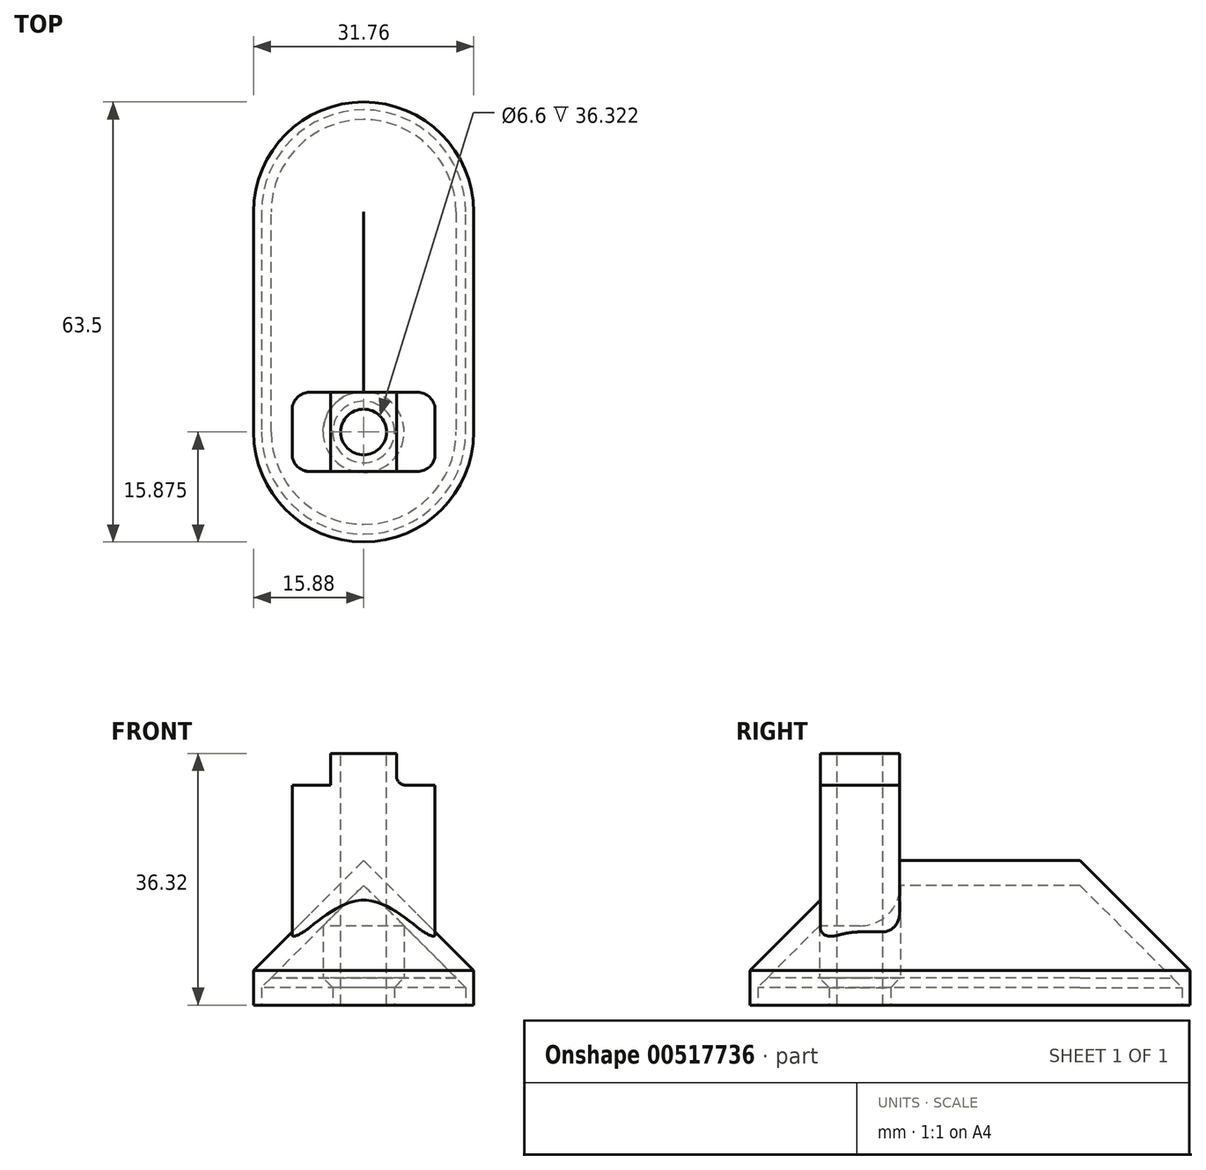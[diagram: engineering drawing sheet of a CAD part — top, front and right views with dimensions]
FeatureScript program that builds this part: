
annotation { "Feature Type Name" : "Feature", "Feature Type Description" : "" }
export const myFeature = defineFeature(function(context is Context, id is Id, definition is map)
    precondition{}
    {
        {
            var Q0;
            Q0=qCreatedBy(makeId("Top.planeOp"),FACE);
            var sketch = newSketch(context, id + "F0", { "sketchPlane" : qUnion([Q0])});
            skLineSegment(sketch, "E0.left", {"start": v(15.88, -15.88) * mm, "end": v(15.88, 15.88) * mm});
            skLineSegment(sketch, "E0.right", {"start": v(-15.88, -15.88) * mm, "end": v(-15.88, 15.87) * mm});
            skPoint(sketch, "E0.middle", {"position": v(0, 0) * mm});
            skArc(sketch, "E1", {"start": v(-15.88, -15.88) * mm, "mid": v(0, -31.75) * mm, "end": v(15.87, -15.88) * mm});
            skArc(sketch, "E2", {"start": v(15.87, 15.88) * mm, "mid": v(0, 31.75) * mm, "end": v(-15.88, 15.88) * mm});
            skSolve(sketch);
        }
        {
            var Q0;
            Q0=makeQuery(id+"F0.imprint","IMPRINT",FACE,{"disambiguationData":[TD([[makeQuery(id+"F0.imprint","IMPRINT",EDGE,{"derivedFrom":sQuery(id+"F0.wireOp",EDGE,"E0.left")}),1.0]])]});
            extrude(context, id + "F1", {"entities" : qUnion([Q0]), "depth" : 20.87 * mm, "offsetDistance" : 25.4 * mm});
        }
        {
            var Q0;
            Q0=makeQuery(id+"F1.opExtrude","CAP_EDGE",EDGE,{"disambiguationData":[OSD([sQuery(id+"F0.wireOp",EDGE,"E0.left")])],"isStart":false});
            chamfer(context, id + "F2", {"entities" : qUnion([Q0]), "width" : 15.88 * mm, "tangentPropagation" : true});
        }
        {
            var Q0;
            Q0=qCreatedBy(makeId("Top.planeOp"),FACE);
            cPlane(context, id + "F3", {"entities" : qUnion([Q0]), "cplaneType" : CPlaneType.OFFSET, "offset" : 31.75 * mm, "width" : 152.4 * mm, "height" : 152.4 * mm});
        }
        {
            var Q0;
            Q0=makeQuery(id+"F1.opExtrude","CAP_FACE",FACE,{"disambiguationData":[OSD([sQuery(id+"F0.wireOp",EDGE,"E0.left"),sQuery(id+"F0.wireOp",EDGE,"E0.right"),sQuery(id+"F0.wireOp",EDGE,"E1"),sQuery(id+"F0.wireOp",EDGE,"E2")])],"isStart":true});
            shell(context, id + "F4", {"entities" : qUnion([Q0]), "thickness" : 2.54 * mm});
        }
        {
            var Q0;
            Q0=qCreatedBy(id+"F3.planeOp",FACE);
            var sketch = newSketch(context, id + "F5", { "sketchPlane" : qUnion([Q0])});
            skLineSegment(sketch, "E3.bottom", {"start": v(10.31, -21.6) * mm, "end": v(-10.31, -21.6) * mm});
            skLineSegment(sketch, "E3.top", {"start": v(10.31, -10.16) * mm, "end": v(-10.31, -10.16) * mm});
            skLineSegment(sketch, "E3.left", {"start": v(10.31, -21.6) * mm, "end": v(10.31, -10.16) * mm});
            skLineSegment(sketch, "E3.right", {"start": v(-10.31, -21.6) * mm, "end": v(-10.31, -10.16) * mm});
            skPoint(sketch, "E3.middle", {"position": v(0, -15.88) * mm});
            skSolve(sketch);
        }
        {
            var Q0;
            Q0=makeQuery(id+"F5.imprint","IMPRINT",FACE,{"disambiguationData":[TD([[makeQuery(id+"F5.imprint","IMPRINT",EDGE,{"derivedFrom":sQuery(id+"F5.wireOp",EDGE,"E3.bottom")}),-1.0]])]});
            extrude(context, id + "F6", {"entities" : qUnion([Q0]), "operationType" : NewBodyOperationType.ADD, "endBound" : BoundingType.UP_TO_NEXT, "oppositeDirection" : true, "depth" : 25.4 * mm, "offsetDistance" : 25.4 * mm});
        }
        {
            var Q0;
            Q0=makeQuery(id+"F6.opExtrude","CAP_FACE",FACE,{"disambiguationData":[OSD([sQuery(id+"F5.wireOp",EDGE,"E3.bottom"),sQuery(id+"F5.wireOp",EDGE,"E3.top"),sQuery(id+"F5.wireOp",EDGE,"E3.left"),sQuery(id+"F5.wireOp",EDGE,"E3.right")])],"isStart":true});
            var sketch = newSketch(context, id + "F7", { "sketchPlane" : qUnion([Q0])});
            skLineSegment(sketch, "E4.bottom", {"start": v(4.76, -10.16) * mm, "end": v(-4.76, -10.16) * mm});
            skLineSegment(sketch, "E4.top", {"start": v(4.76, -21.6) * mm, "end": v(-4.76, -21.6) * mm});
            skLineSegment(sketch, "E4.left", {"start": v(4.76, -10.16) * mm, "end": v(4.76, -21.6) * mm});
            skLineSegment(sketch, "E4.right", {"start": v(-4.76, -10.16) * mm, "end": v(-4.76, -21.6) * mm});
            skPoint(sketch, "E4.middle", {"position": v(0, -15.88) * mm});
            skSolve(sketch);
        }
        {
            var Q0;
            Q0 = qSketchRegion(id + "F7", true);
            extrude(context, id + "F8", {"entities" : qUnion([Q0]), "operationType" : NewBodyOperationType.ADD, "depth" : 4.57 * mm, "offsetDistance" : 25.4 * mm});
        }
        {
            var Q0;
            Q0=makeQuery(id+"F8.opExtrude","CAP_FACE",FACE,{"disambiguationData":[OSD([sQuery(id+"F7.wireOp",EDGE,"E4.bottom"),sQuery(id+"F7.wireOp",EDGE,"E4.top"),sQuery(id+"F7.wireOp",EDGE,"E4.left"),sQuery(id+"F7.wireOp",EDGE,"E4.right")])],"isStart":false});
            var sketch = newSketch(context, id + "F9", { "sketchPlane" : qUnion([Q0])});
            skCircle(sketch, "E5", {"center": v(0, -15.88) * mm, "radius": 3.3 * mm});
            skLineSegment(sketch, "E6", {"start": v(-4.76, -21.6) * mm, "end": v(4.76, -10.16) * mm, "construction": true});
            skSolve(sketch);
        }
        {
            var Q0;
            Q0 = qSketchRegion(id + "F9", true);
            extrude(context, id + "F10", {"entities" : qUnion([Q0]), "operationType" : NewBodyOperationType.REMOVE, "endBound" : BoundingType.THROUGH_ALL, "oppositeDirection" : true, "depth" : 25.4 * mm, "offsetDistance" : 25.4 * mm});
        }
        {
            var Q0;
            Q0=makeQuery(id+"F6.opExtrude","CAP_EDGE",EDGE,{"disambiguationData":[OSD([sQuery(id+"F5.wireOp",EDGE,"E3.right")]),topologyDisambiguationEdgeConnected([makeQuery(id+"F2.opChamfer","BLEND_FACE",FACE,{"disambiguationData":[OSD([sQuery(id+"F0.wireOp",EDGE,"E1")])]})])],"isStart":false});
            var Q1;
            Q1=makeQuery(id+"F6.opExtrude","CAP_EDGE",EDGE,{"disambiguationData":[OSD([sQuery(id+"F5.wireOp",EDGE,"E3.bottom")])],"isStart":false});
            var Q2;
            Q2=makeQuery(id+"F6.opExtrude","CAP_EDGE",EDGE,{"disambiguationData":[OSD([sQuery(id+"F5.wireOp",EDGE,"E3.left")]),topologyDisambiguationEdgeConnected([makeQuery(id+"F2.opChamfer","BLEND_FACE",FACE,{"disambiguationData":[OSD([sQuery(id+"F0.wireOp",EDGE,"E1")])]})])],"isStart":false});
            var Q3;
            Q3=makeQuery(id+"F6.opExtrude","CAP_EDGE",EDGE,{"disambiguationData":[OSD([sQuery(id+"F5.wireOp",EDGE,"E3.top")]),topologyDisambiguationEdgeConnected([makeQuery(id+"F2.opChamfer","BLEND_FACE",FACE,{"disambiguationData":[OSD([sQuery(id+"F0.wireOp",EDGE,"E0.left")])]})])],"isStart":false});
            var Q4;
            Q4=makeQuery(id+"F6.opExtrude","CAP_EDGE",EDGE,{"disambiguationData":[OSD([sQuery(id+"F5.wireOp",EDGE,"E3.top")]),topologyDisambiguationEdgeConnected([makeQuery(id+"F2.opChamfer","BLEND_FACE",FACE,{"disambiguationData":[OSD([sQuery(id+"F0.wireOp",EDGE,"E0.right")])]})])],"isStart":false});
            var Q5;
            Q5=makeQuery(id+"F6.opExtrude","SWEPT_EDGE",EDGE,{"disambiguationData":[OSD([sQuery(id+"F5.wireOp",EDGE,"E3.bottom"),sQuery(id+"F5.wireOp",EDGE,"E3.left")])]});
            var Q6;
            Q6=makeQuery(id+"F6.opExtrude","SWEPT_EDGE",EDGE,{"disambiguationData":[OSD([sQuery(id+"F5.wireOp",EDGE,"E3.top"),sQuery(id+"F5.wireOp",EDGE,"E3.left")])]});
            var Q7;
            Q7=makeQuery(id+"F6.opExtrude","SWEPT_EDGE",EDGE,{"disambiguationData":[OSD([sQuery(id+"F5.wireOp",EDGE,"E3.bottom"),sQuery(id+"F5.wireOp",EDGE,"E3.right")])]});
            var Q8;
            Q8=makeQuery(id+"F6.opExtrude","SWEPT_EDGE",EDGE,{"disambiguationData":[OSD([sQuery(id+"F5.wireOp",EDGE,"E3.top"),sQuery(id+"F5.wireOp",EDGE,"E3.right")])]});
            fillet(context, id + "F11", {"entities" : qUnion([Q0, Q1, Q2, Q3, Q4, Q5, Q6, Q7, Q8]), "radius" : 2.54 * mm, "tangentPropagation" : true, "allowEdgeOverflow" : false});
        }
        {
            var Q0;
            Q0=makeQuery(id+"F1.opExtrude","CAP_FACE",FACE,{"disambiguationData":[OSD([sQuery(id+"F0.wireOp",EDGE,"E0.left"),sQuery(id+"F0.wireOp",EDGE,"E0.right"),sQuery(id+"F0.wireOp",EDGE,"E1"),sQuery(id+"F0.wireOp",EDGE,"E2")])],"isStart":true});
            var sketch = newSketch(context, id + "F12", { "sketchPlane" : qUnion([Q0])});
            skCircle(sketch, "E7", {"center": v(0, 15.88) * mm, "radius": 3.3 * mm});
            skCircle(sketch, "E8", {"center": v(0, 15.88) * mm, "radius": 5.84 * mm});
            skSolve(sketch);
        }
        {
            var Q0;
            Q0=makeQuery(id+"F12.imprint","IMPRINT",FACE,{"disambiguationData":[TD([[makeQuery(id+"F12.imprint","IMPRINT",EDGE,{"derivedFrom":sQuery(id+"F12.wireOp",EDGE,"E7")}),-1.0]])]});
            extrude(context, id + "F13", {"entities" : qUnion([Q0]), "operationType" : NewBodyOperationType.ADD, "endBound" : BoundingType.UP_TO_NEXT, "oppositeDirection" : true, "depth" : 25.4 * mm, "offsetDistance" : 25.4 * mm});
        }
        {
            var Q0;
            Q0=makeQuery(id+"F0.imprint","IMPRINT",FACE,{"disambiguationData":[TD([[makeQuery(id+"F0.imprint","IMPRINT",EDGE,{"derivedFrom":sQuery(id+"F0.wireOp",EDGE,"E0.left")}),1.0]])]});
            var sketch = newSketch(context, id + "F14", { "sketchPlane" : qUnion([Q0])});
            skLineSegment(sketch, "E9", {"start": v(-14.73, 15.88) * mm, "end": v(-14.73, -15.88) * mm});
            skArc(sketch, "E10", {"start": v(-14.73, -15.88) * mm, "mid": v(0, -30.6) * mm, "end": v(14.73, -15.88) * mm});
            skLineSegment(sketch, "E11", {"start": v(14.73, -15.88) * mm, "end": v(14.73, 15.88) * mm});
            skArc(sketch, "E12", {"start": v(14.73, 15.88) * mm, "mid": v(0, 30.6) * mm, "end": v(-14.73, 15.88) * mm});
            skCircle(sketch, "E13", {"center": v(0, -15.88) * mm, "radius": 4.45 * mm});
            skSolve(sketch);
        }
        {
            var Q0;
            Q0 = qSketchRegion(id + "F14", true);
            extrude(context, id + "F15", {"entities" : qUnion([Q0]), "operationType" : NewBodyOperationType.REMOVE, "depth" : 2.54 * mm, "offsetDistance" : 25.4 * mm});
        }
        {
            var Q0;
            {var subQ0=sQuery(id+"F0.wireOp",EDGE,"E0.right");Q0=makeQuery(id+"F15.boolean.opBoolean","INTERSECT",EDGE,{"derivedFrom":[makeQuery(id+"F4.opShell","OFFSET_FACE",FACE,{"disambiguationData":[OSD([subQ0]),TDD([makeQuery(id+"F1.opExtrude","SWEPT_FACE",FACE,{"disambiguationData":[OSD([subQ0])]})])]}),makeQuery(id+"F15.opExtrude","CAP_FACE",FACE,{"disambiguationData":[OSD([sQuery(id+"F14.wireOp",EDGE,"E9"),sQuery(id+"F14.wireOp",EDGE,"E10"),sQuery(id+"F14.wireOp",EDGE,"E11"),sQuery(id+"F14.wireOp",EDGE,"E12"),sQuery(id+"F14.wireOp",EDGE,"E13")])],"isStart":false})]});}
            var Q1;
            Q1=makeQuery(id+"F15.boolean.opBoolean","INTERSECT",EDGE,{"derivedFrom":[makeQuery(id+"F13.opExtrude","SWEPT_FACE",FACE,{"disambiguationData":[OSD([sQuery(id+"F12.wireOp",EDGE,"E8")])]}),makeQuery(id+"F15.opExtrude","CAP_FACE",FACE,{"disambiguationData":[OSD([sQuery(id+"F14.wireOp",EDGE,"E9"),sQuery(id+"F14.wireOp",EDGE,"E10"),sQuery(id+"F14.wireOp",EDGE,"E11"),sQuery(id+"F14.wireOp",EDGE,"E12"),sQuery(id+"F14.wireOp",EDGE,"E13")])],"isStart":false})]});
            chamfer(context, id + "F16", {"entities" : qUnion([Q0, Q1]), "width" : 1.4 * mm, "tangentPropagation" : true});
        }
        {
            var Q0;
            Q0=makeQuery(id+"F8.opExtrude","CAP_EDGE",EDGE,{"disambiguationData":[OSD([sQuery(id+"F7.wireOp",EDGE,"E4.left")])],"isStart":true});
            var Q1;
            Q1=makeQuery(id+"F8.opExtrude","CAP_EDGE",EDGE,{"disambiguationData":[OSD([sQuery(id+"F7.wireOp",EDGE,"E4.right")])],"isStart":true});
            fillet(context, id + "F17", {"entities" : qUnion([Q0, Q1]), "radius" : 1.27 * mm, "tangentPropagation" : true, "allowEdgeOverflow" : false});
        }
    });
